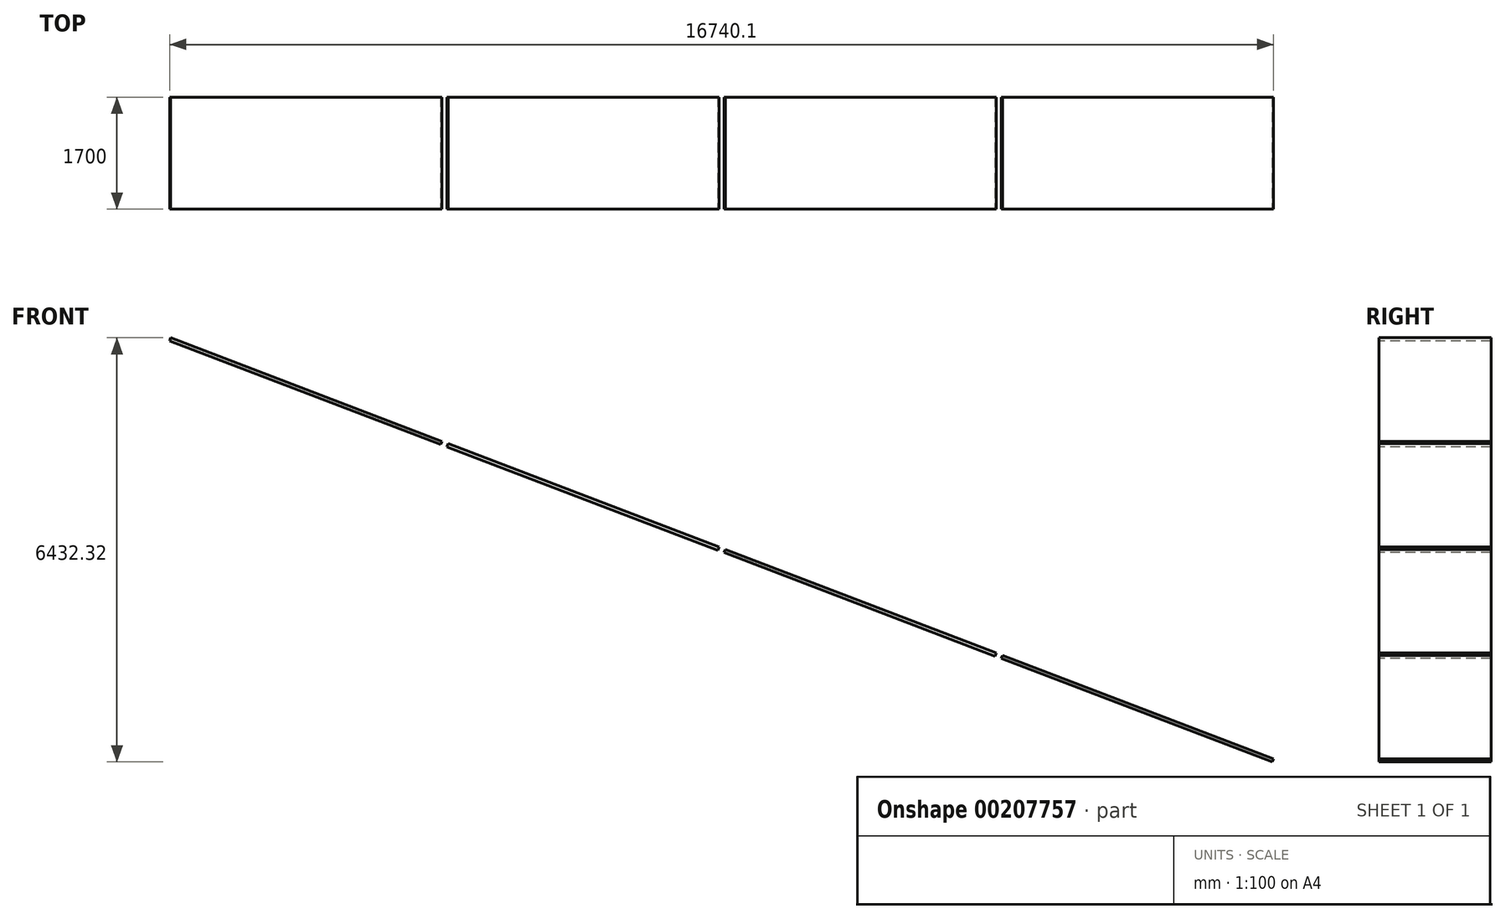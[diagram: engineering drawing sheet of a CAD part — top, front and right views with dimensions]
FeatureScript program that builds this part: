
annotation { "Feature Type Name" : "Feature", "Feature Type Description" : "" }
export const myFeature = defineFeature(function(context is Context, id is Id, definition is map)
    precondition{}
    {
        {
            var Q0;
            Q0=qCreatedBy(makeId("Top.planeOp"),FACE);
            cPlane(context, id + "F0", {"entities" : qUnion([Q0]), "cplaneType" : CPlaneType.OFFSET, "offset" : 6671 * mm, "width" : 150 * mm, "height" : 150 * mm});
        }
        {
            var Q0;
            Q0=qCreatedBy(id+"F0.planeOp",FACE);
            var sketch = newSketch(context, id + "F1", { "sketchPlane" : qUnion([Q0])});
            skLineSegment(sketch, "E0.bottom", {"start": v(-1850, 1900) * mm, "end": v(1850, 1900) * mm, "construction": true});
            skLineSegment(sketch, "E0.top", {"start": v(-1850, -1900) * mm, "end": v(1850, -1900) * mm, "construction": true});
            skLineSegment(sketch, "E0.left", {"start": v(-1850, 1900) * mm, "end": v(-1850, -1900) * mm, "construction": true});
            skLineSegment(sketch, "E0.right", {"start": v(1850, 1900) * mm, "end": v(1850, -1900) * mm, "construction": true});
            skSolve(sketch);
        }
        {
            var Q0;
            Q0=sQuery(id+"F1.wireOp",EDGE,"E0.right");
            var Q1;
            Q1=qCreatedBy(id+"F0.planeOp",FACE);
            cPlane(context, id + "F2", {"entities" : qUnion([Q0, Q1]), "cplaneType" : CPlaneType.LINE_ANGLE, "offset" : 25 * mm, "angle" : 20.9 * degree, "oppositeDirection" : true, "width" : 150 * mm, "height" : 150 * mm});
        }
        {
            var Q0;
            Q0=qCreatedBy(id+"F2.planeOp",FACE);
            var sketch = newSketch(context, id + "F3", { "sketchPlane" : qUnion([Q0])});
            skLineSegment(sketch, "E1.bottom", {"start": v(-644.4, -850) * mm, "end": v(3755.6, -850) * mm});
            skLineSegment(sketch, "E1.top", {"start": v(-644.4, 850) * mm, "end": v(3755.6, 850) * mm});
            skLineSegment(sketch, "E1.left", {"start": v(-644.4, -850) * mm, "end": v(-644.4, 850) * mm});
            skLineSegment(sketch, "E1.right", {"start": v(3755.6, -850) * mm, "end": v(3755.6, 850) * mm});
            skLineSegment(sketch, "E2.bottom", {"start": v(3855.6, -850) * mm, "end": v(8255.6, -850) * mm});
            skLineSegment(sketch, "E2.top", {"start": v(3855.6, 850) * mm, "end": v(8255.6, 850) * mm});
            skLineSegment(sketch, "E2.left", {"start": v(3855.6, -850) * mm, "end": v(3855.6, 850) * mm});
            skLineSegment(sketch, "E2.right", {"start": v(8255.6, -850) * mm, "end": v(8255.6, 850) * mm});
            skLineSegment(sketch, "E3.bottom", {"start": v(8355.6, -850) * mm, "end": v(12755.6, -850) * mm});
            skLineSegment(sketch, "E3.top", {"start": v(8355.6, 850) * mm, "end": v(12755.6, 850) * mm});
            skLineSegment(sketch, "E3.left", {"start": v(8355.6, -850) * mm, "end": v(8355.6, 850) * mm});
            skLineSegment(sketch, "E3.right", {"start": v(12755.6, -850) * mm, "end": v(12755.6, 850) * mm});
            skLineSegment(sketch, "E4.bottom", {"start": v(12855.6, -850) * mm, "end": v(17255.6, -850) * mm});
            skLineSegment(sketch, "E4.top", {"start": v(12855.6, 850) * mm, "end": v(17255.6, 850) * mm});
            skLineSegment(sketch, "E4.left", {"start": v(12855.6, -850) * mm, "end": v(12855.6, 850) * mm});
            skLineSegment(sketch, "E4.right", {"start": v(17255.6, -850) * mm, "end": v(17255.6, 850) * mm});
            skSolve(sketch);
        }
        {
            var Q0;
            Q0 = qSketchRegion(id + "F3", true);
            extrude(context, id + "F4", {"entities" : qUnion([Q0]), "depth" : 50 * mm, "offsetDistance" : 25 * mm});
        }
    });
